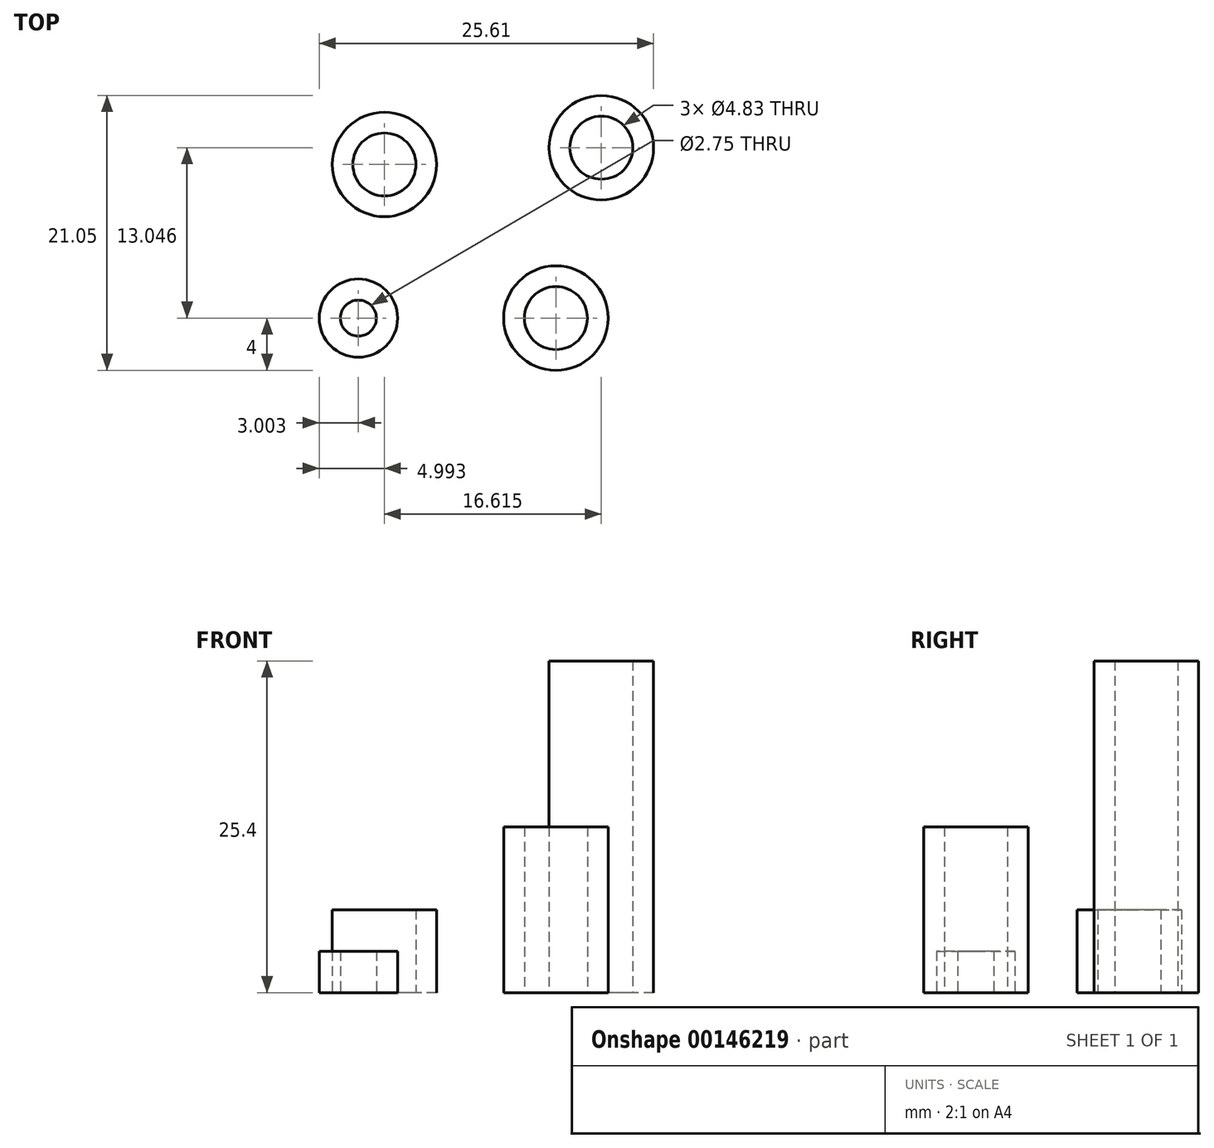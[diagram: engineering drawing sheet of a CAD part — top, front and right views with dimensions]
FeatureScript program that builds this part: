
annotation { "Feature Type Name" : "Feature", "Feature Type Description" : "" }
export const myFeature = defineFeature(function(context is Context, id is Id, definition is map)
    precondition{}
    {
        {
            var Q0;
            Q0=qCreatedBy(makeId("Top.planeOp"),FACE);
            var sketch = newSketch(context, id + "F0", { "sketchPlane" : qUnion([Q0])});
            skCircle(sketch, "E0", {"center": v(3.48, 13.05) * mm, "radius": 4 * mm});
            skCircle(sketch, "E1", {"center": v(3.48, 13.05) * mm, "radius": 2.41 * mm});
            skSolve(sketch);
        }
        {
            var Q0;
            Q0=qCreatedBy(makeId("Top.planeOp"),FACE);
            var sketch = newSketch(context, id + "F1", { "sketchPlane" : qUnion([Q0])});
            skCircle(sketch, "E2", {"center": v(0, 0) * mm, "radius": 4 * mm});
            skCircle(sketch, "E3", {"center": v(0, 0) * mm, "radius": 2.41 * mm});
            skSolve(sketch);
        }
        {
            var Q0;
            Q0=qCreatedBy(makeId("Top.planeOp"),FACE);
            var sketch = newSketch(context, id + "F2", { "sketchPlane" : qUnion([Q0])});
            skCircle(sketch, "E4", {"center": v(-13.14, 11.77) * mm, "radius": 4 * mm});
            skCircle(sketch, "E5", {"center": v(-13.14, 11.77) * mm, "radius": 2.41 * mm});
            skSolve(sketch);
        }
        {
            var Q0;
            Q0=qCreatedBy(makeId("Top.planeOp"),FACE);
            var sketch = newSketch(context, id + "F3", { "sketchPlane" : qUnion([Q0])});
            skCircle(sketch, "E6", {"center": v(-15.13, 0) * mm, "radius": 1.38 * mm});
            skCircle(sketch, "E7", {"center": v(-15.13, 0) * mm, "radius": 3 * mm});
            skSolve(sketch);
        }
        {
            var Q0;
            Q0 = qSketchRegion(id + "F0", true);
            extrude(context, id + "F4", {"entities" : qUnion([Q0]), "depth" : 25.4 * mm});
        }
        {
            var Q0;
            Q0 = qSketchRegion(id + "F1", true);
            extrude(context, id + "F5", {"entities" : qUnion([Q0]), "depth" : 12.7 * mm});
        }
        {
            var Q0;
            Q0 = qSketchRegion(id + "F2", true);
            extrude(context, id + "F6", {"entities" : qUnion([Q0]), "depth" : 6.35 * mm});
        }
        {
            var Q0;
            Q0 = qSketchRegion(id + "F3", true);
            extrude(context, id + "F7", {"entities" : qUnion([Q0]), "depth" : 3.17 * mm});
        }
    });
